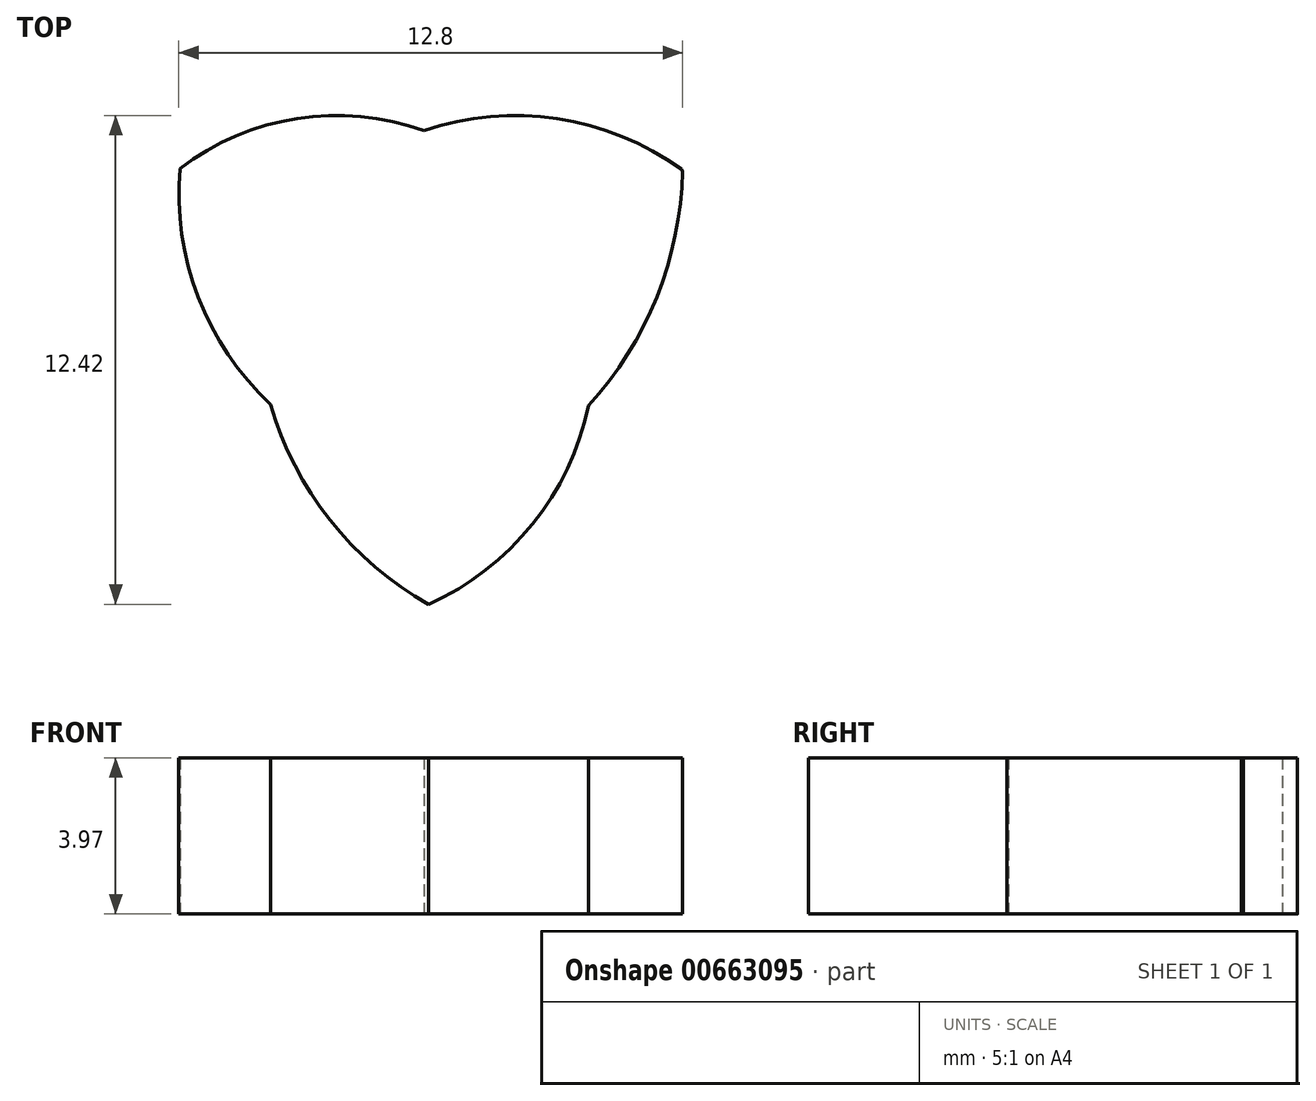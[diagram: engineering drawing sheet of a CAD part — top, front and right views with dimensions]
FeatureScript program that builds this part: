
annotation { "Feature Type Name" : "Feature", "Feature Type Description" : "" }
export const myFeature = defineFeature(function(context is Context, id is Id, definition is map)
    precondition{}
    {
        {
            var Q0;
            Q0=qCreatedBy(makeId("Top.planeOp"),FACE);
            var sketch = newSketch(context, id + "F0", { "sketchPlane" : qUnion([Q0])});
            skPoint(sketch, "E0.center", {"position": v(0, 0) * mm});
            skLineSegment(sketch, "E1", {"start": v(-12.37, 4.64) * mm, "end": v(-12.37, 4.57) * mm});
            skLineSegment(sketch, "E2", {"start": v(7.76, 1.05) * mm, "end": v(7.76, 1.05) * mm});
            skLineSegment(sketch, "E3", {"start": v(8, -1.42) * mm, "end": v(8, -1.42) * mm});
            skLineSegment(sketch, "E4", {"start": v(6.33, 3.65) * mm, "end": v(6.36, 3.6) * mm});
            skArc(sketch, "E5", {"start": v(-0.1, -7.4) * mm, "mid": v(2.54, -5.36) * mm, "end": v(3.97, -2.35) * mm});
            skArc(sketch, "E6", {"start": v(3.97, -2.35) * mm, "mid": v(5.7, 0.4) * mm, "end": v(6.36, 3.6) * mm});
            skArc(sketch, "E7", {"start": v(-6.41, 3.67) * mm, "mid": v(-5.95, 0.4) * mm, "end": v(-4.1, -2.33) * mm});
            skArc(sketch, "E8", {"start": v(-4.1, -2.33) * mm, "mid": v(-2.6, -5.26) * mm, "end": v(-0.1, -7.4) * mm});
            skArc(sketch, "E9", {"start": v(-0.21, 4.63) * mm, "mid": v(-3.44, 4.94) * mm, "end": v(-6.41, 3.67) * mm});
            skArc(sketch, "E10", {"start": v(6.33, 3.65) * mm, "mid": v(3.18, 4.94) * mm, "end": v(-0.21, 4.63) * mm});
            skSolve(sketch);
        }
        {
            var Q0;
            Q0=makeQuery(id+"F0.imprint","IMPRINT",FACE,{"disambiguationData":[TD([[makeQuery(id+"F0.imprint","IMPRINT",EDGE,{"derivedFrom":sQuery(id+"F0.wireOp",EDGE,"E4")}),-1.0]])]});
            extrude(context, id + "F1", {"entities" : qUnion([Q0]), "depth" : 3.97 * mm, "offsetDistance" : 25.4 * mm});
        }
    });
